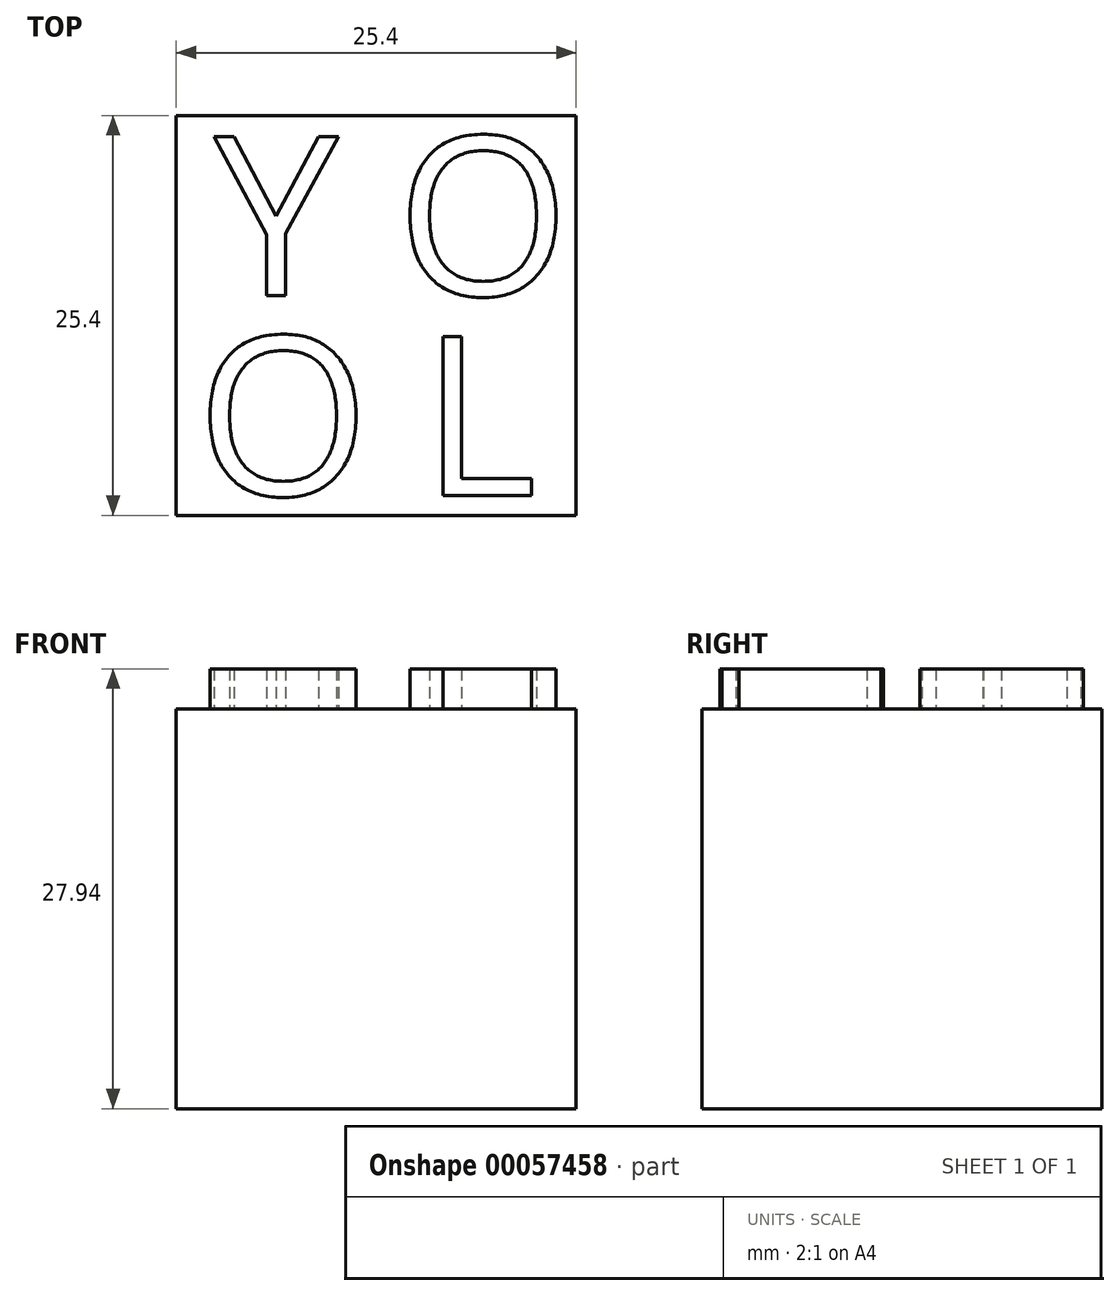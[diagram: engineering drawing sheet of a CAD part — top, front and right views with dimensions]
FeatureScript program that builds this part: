
annotation { "Feature Type Name" : "Feature", "Feature Type Description" : "" }
export const myFeature = defineFeature(function(context is Context, id is Id, definition is map)
    precondition{}
    {
        {
            var Q0;
            Q0=qCreatedBy(makeId("Top.planeOp"),FACE);
            var sketch = newSketch(context, id + "F0", { "sketchPlane" : qUnion([Q0])});
            skLineSegment(sketch, "E0.rect.bottom", {"start": v(12.7, -12.7) * mm, "end": v(-12.7, -12.7) * mm});
            skLineSegment(sketch, "E0.rect.top", {"start": v(12.7, 12.7) * mm, "end": v(-12.7, 12.7) * mm});
            skLineSegment(sketch, "E0.rect.left", {"start": v(12.7, -12.7) * mm, "end": v(12.7, 12.7) * mm});
            skLineSegment(sketch, "E0.rect.right", {"start": v(-12.7, -12.7) * mm, "end": v(-12.7, 12.7) * mm});
            skPoint(sketch, "E0.rect.middle", {"position": v(0, 0) * mm});
            skSolve(sketch);
        }
        {
            var Q0;
            Q0 = qSketchRegion(id + "F0", true);
            extrude(context, id + "F1", {"entities" : qUnion([Q0]), "depth" : 25.4 * mm});
        }
        {
            var Q0;
            Q0=makeQuery(id+"F1.opExtrude","CAP_FACE",FACE,{"disambiguationData":[OSD([sQuery(id+"F0.wireOp",EDGE,"E0.rect.bottom"),sQuery(id+"F0.wireOp",EDGE,"E0.rect.top"),sQuery(id+"F0.wireOp",EDGE,"E0.rect.left"),sQuery(id+"F0.wireOp",EDGE,"E0.rect.right")])],"isStart":false});
            var sketch = newSketch(context, id + "F2", { "sketchPlane" : qUnion([Q0])});
            skText(sketch, "E1", { "text": "Y", "fontName": "OpenSans-Regular.ttf"});
            skText(sketch, "E2", { "text": "O", "fontName": "OpenSans-Regular.ttf"});
            skText(sketch, "E3", { "text": "L", "fontName": "OpenSans-Regular.ttf"});
            skText(sketch, "E4", { "text": "O", "fontName": "OpenSans-Regular.ttf"});
            const initialGuessF2  = {"E1": [-0.0103, 0.00127, 1, 0, 0.01016], "E2": [0.00129, 0.00127, 1, 0, 0.01016], "E3": [0.00285, -0.01143, 1, 0, 0.01016], "E4": [-0.01141, -0.01143, 1, 0, 0.01016]};
            skSetInitialGuess(sketch, initialGuessF2);
            skSolve(sketch);
        }
        {
            var Q0;
            Q0 = qSketchRegion(id + "F2", true);
            extrude(context, id + "F3", {"entities" : qUnion([Q0]), "operationType" : NewBodyOperationType.ADD, "depth" : 2.54 * mm});
        }
    });
